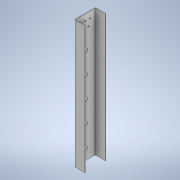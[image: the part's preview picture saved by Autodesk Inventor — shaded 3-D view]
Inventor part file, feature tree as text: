
AUTODESK INVENTOR PART (.ipt)
format: ipt  version: 2022 (Build 260153000, 153)  size: 207,360 bytes
history: native  units: mm
features: sheet_metal_op x3, sketch x3, other x3, projected_geometry x2, extrude x1
ambient origin geometry x8: Origin, YZ Plane, XZ Plane, XY Plane, X Axis, Y Axis, Z Axis, Center Point
bodies: Solid1 (feature_tree)
feature tree (12):
  sheet_metal_op  "Contour Flange1"
  extrude  "Extrusion3"  Depth=25.0mm
  sketch  "Sketch1"  dims[d0=50.0mm d1=25.0mm]
  other  "Plate1"
  sheet_metal_op  "Bend1"
  sheet_metal_op  "Corner1"
  sketch  "Sketch2"  dims[d2=25.0mm]
  projected_geometry  "Projected Loop1"
  sketch  "Sketch8"  dims[d3=1.5mm d4=1.5mm d5=0.75mm d6=3.0mm d7=1.5mm d8=300.0mm d9=1.5mm d10=0.5mm d11=6.0mm d12=1.5mm d13=1.5mm d14=10.2mm d15=25.0mm d16=22.0mm d17=50.0mm d19=50.0mm d20=10.0mm d22=10.0mm d24=1.5mm d25=0.0mm d33=44.0mm d34=3.25mm d35=3.25mm d36=3.25mm d37=3.25mm d38=3.25mm d39=44.0mm d40=14.666667mm d41=14.666667mm d42=14.666667mm d43=14.666667mm d44=14.666667mm d45=14.666667mm d46=14.666667mm d47=11.0mm d48=11.0mm d49=11.0mm d50=10.0mm d51=0.0mm]
  projected_geometry  "Projected Loop9"
  other  "Cut1"
  other  "Definition1"
